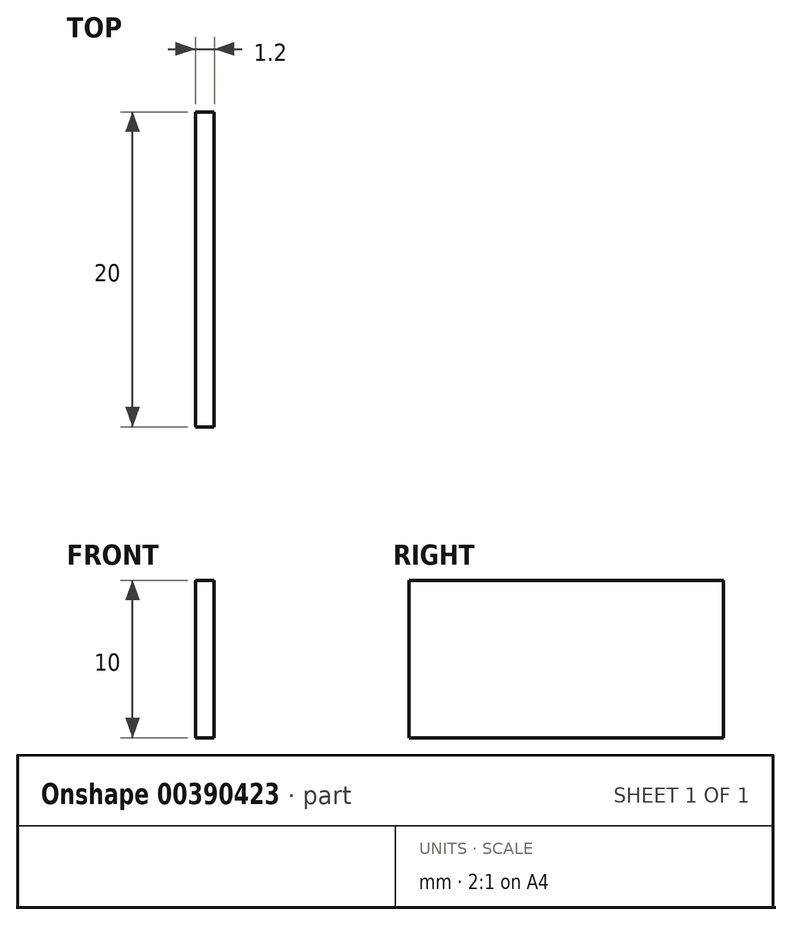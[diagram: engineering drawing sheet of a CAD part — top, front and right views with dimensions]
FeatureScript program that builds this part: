
annotation { "Feature Type Name" : "Feature", "Feature Type Description" : "" }
export const myFeature = defineFeature(function(context is Context, id is Id, definition is map)
    precondition{}
    {
        {
            assignVariable(context, id + "F0", {"name" : "depth", "anyValue" : 20});
        }
        {
            var Q0;
            Q0=qCreatedBy(makeId("Front.planeOp"),FACE);
            var sketch = newSketch(context, id + "F1", { "sketchPlane" : qUnion([Q0])});
            skLineSegment(sketch, "E0.bottom", {"start": v(-0.6, 5) * mm, "end": v(0.6, 5) * mm});
            skLineSegment(sketch, "E0.top", {"start": v(-0.6, -5) * mm, "end": v(0.6, -5) * mm});
            skLineSegment(sketch, "E0.left", {"start": v(-0.6, 5) * mm, "end": v(-0.6, -5) * mm});
            skLineSegment(sketch, "E0.right", {"start": v(0.6, 5) * mm, "end": v(0.6, -5) * mm});
            skPoint(sketch, "E0.middle", {"position": v(0, 0) * mm});
            skSolve(sketch);
        }
        {
            var Q0;
            Q0=makeQuery(id+"F1.imprint","IMPRINT",FACE,{"disambiguationData":[TD([[makeQuery(id+"F1.imprint","IMPRINT",EDGE,{"derivedFrom":sQuery(id+"F1.wireOp",EDGE,"E0.bottom")}),-1.0]])]});
            extrude(context, id + "F2", {"entities" : qUnion([Q0]), "endBound" : BoundingType.SYMMETRIC, "depth" : (getVariable(context, 'depth')) * mm});
        }
    });
